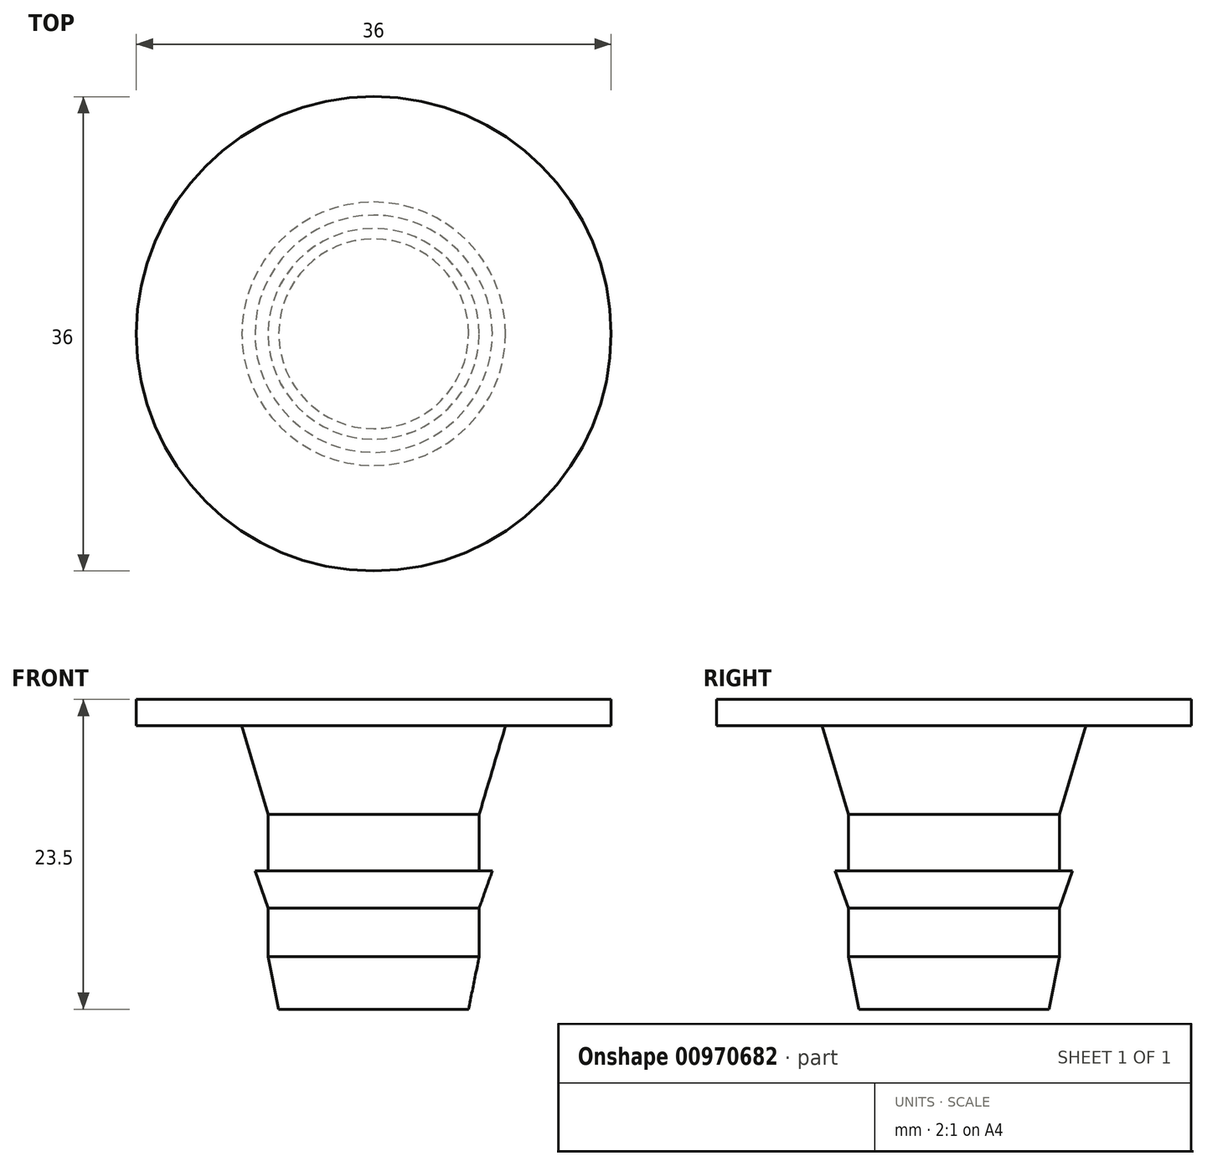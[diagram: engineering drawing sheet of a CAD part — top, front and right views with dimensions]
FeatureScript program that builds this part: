
annotation { "Feature Type Name" : "Feature", "Feature Type Description" : "" }
export const myFeature = defineFeature(function(context is Context, id is Id, definition is map)
    precondition{}
    {
        {
            var Q0;
            Q0=qCreatedBy(makeId("Front.planeOp"),FACE);
            var sketch = newSketch(context, id + "F0", { "sketchPlane" : qUnion([Q0])});
            skLineSegment(sketch, "E0", {"start": v(-8, 6.5) * mm, "end": v(-8, 21.5) * mm});
            skLineSegment(sketch, "E1", {"start": v(-8, 21.5) * mm, "end": v(-18, 21.5) * mm});
            skLineSegment(sketch, "E2", {"start": v(-18, 21.5) * mm, "end": v(-18, 23.5) * mm});
            skLineSegment(sketch, "E3", {"start": v(0, 23.5) * mm, "end": v(0, 0) * mm});
            skLineSegment(sketch, "E4", {"start": v(-18, 23.5) * mm, "end": v(0, 23.5) * mm});
            skLineSegment(sketch, "E5", {"start": v(0, 0) * mm, "end": v(-7.2, 0) * mm});
            skLineSegment(sketch, "E6", {"start": v(-7.2, 0) * mm, "end": v(-8, 4) * mm});
            skLineSegment(sketch, "E7", {"start": v(-8, 10.5) * mm, "end": v(-9, 10.5) * mm});
            skLineSegment(sketch, "E8", {"start": v(-9, 10.5) * mm, "end": v(-8, 7.67) * mm});
            skLineSegment(sketch, "E9", {"start": v(-8, 6.5) * mm, "end": v(-8, 4) * mm});
            skLineSegment(sketch, "E10", {"start": v(-8, 21.5) * mm, "end": v(-10, 21.5) * mm});
            skLineSegment(sketch, "E11", {"start": v(-10, 21.5) * mm, "end": v(-8, 14.78) * mm});
            skSolve(sketch);
        }
        {
            var Q0;
            Q0=qSketchRegion(id+"F0",true);
            var Q1;
            Q1=sQuery(id+"F0.wireOp",EDGE,"E3");
            revolve(context, id + "F1", {"surfaceOperationType" : NewSurfaceOperationType.NEW, "entities" : qUnion([Q0]), "axis" : qUnion([Q1]), "revolveType" : RevolveType.FULL});
        }
    });
